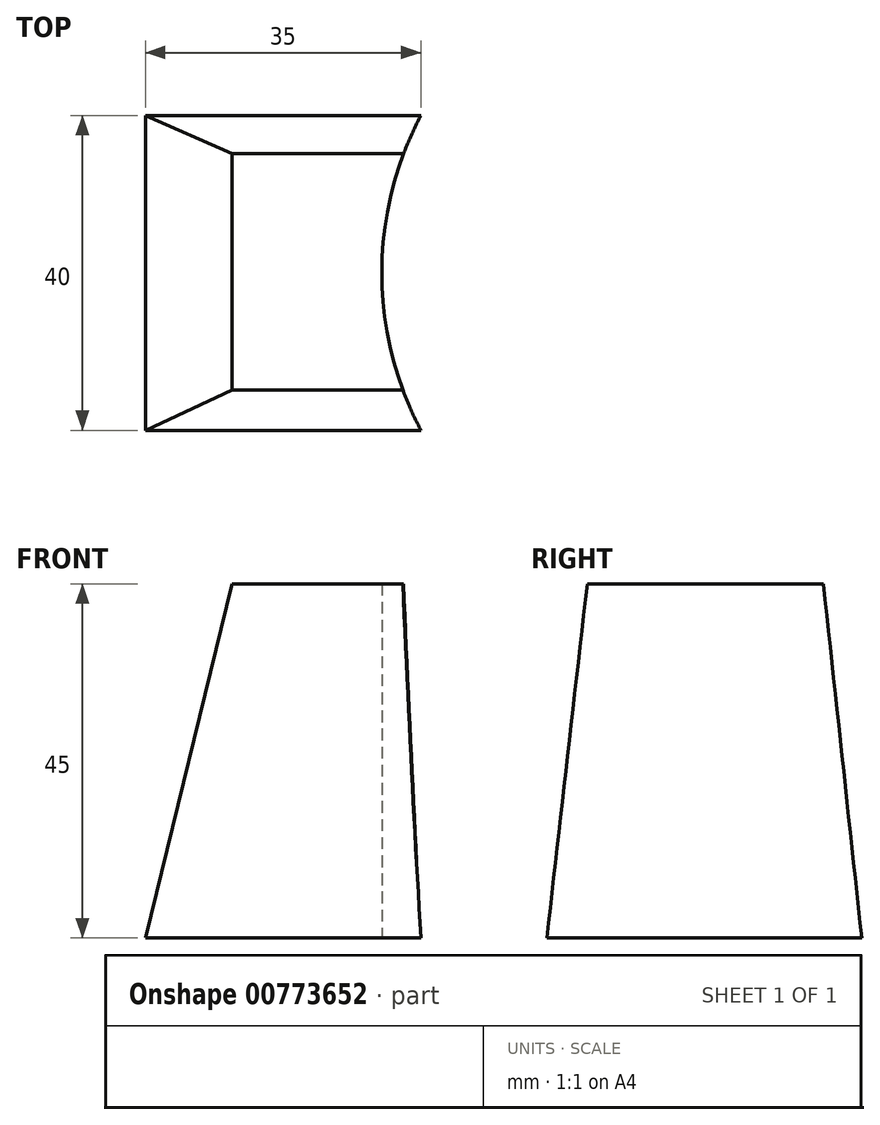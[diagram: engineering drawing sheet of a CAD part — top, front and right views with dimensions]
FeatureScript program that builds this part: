
annotation { "Feature Type Name" : "Feature", "Feature Type Description" : "" }
export const myFeature = defineFeature(function(context is Context, id is Id, definition is map)
    precondition{}
    {
        {
            var Q0;
            Q0=qCreatedBy(makeId("Right.planeOp"),FACE);
            var sketch = newSketch(context, id + "F0", { "sketchPlane" : qUnion([Q0])});
            skLineSegment(sketch, "E0", {"start": v(0, 0) * mm, "end": v(40, 0) * mm});
            skLineSegment(sketch, "E1", {"start": v(40, 0) * mm, "end": v(35.13, 45) * mm});
            skLineSegment(sketch, "E2", {"start": v(35.13, 45) * mm, "end": v(5.13, 45) * mm});
            skLineSegment(sketch, "E3", {"start": v(5.13, 45) * mm, "end": v(0, 0) * mm});
            skSolve(sketch);
        }
        {
            var Q0;
            Q0=makeQuery(id+"F0.imprint","IMPRINT",FACE,{"disambiguationData":[TD([[makeQuery(id+"F0.imprint","IMPRINT",EDGE,{"derivedFrom":sQuery(id+"F0.wireOp",EDGE,"E0")}),1.0]])]});
            extrude(context, id + "F1", {"entities" : qUnion([Q0]), "oppositeDirection" : true, "depth" : 35 * mm, "offsetDistance" : 25.4 * mm});
        }
        {
            var Q0;
            Q0=qCreatedBy(makeId("Front.planeOp"),FACE);
            var sketch = newSketch(context, id + "F2", { "sketchPlane" : qUnion([Q0])});
            skLineSegment(sketch, "E4", {"start": v(-35, 0) * mm, "end": v(-24, 45) * mm});
            skLineSegment(sketch, "E5", {"start": v(-24, 45) * mm, "end": v(-35, 45) * mm});
            skLineSegment(sketch, "E6", {"start": v(-35, 45) * mm, "end": v(-35, 0) * mm});
            skSolve(sketch);
        }
        {
            var Q0;
            Q0=makeQuery(id+"F2.imprint","IMPRINT",FACE,{"disambiguationData":[TD([[makeQuery(id+"F2.imprint","IMPRINT",EDGE,{"derivedFrom":sQuery(id+"F2.wireOp",EDGE,"E4")}),1.0]])]});
            extrude(context, id + "F3", {"entities" : qUnion([Q0]), "operationType" : NewBodyOperationType.REMOVE, "endBound" : BoundingType.THROUGH_ALL, "oppositeDirection" : true, "depth" : 25.4 * mm, "offsetDistance" : 25.4 * mm});
        }
        {
            var Q0;
            Q0=qCreatedBy(makeId("Top.planeOp"),FACE);
            var sketch = newSketch(context, id + "F4", { "sketchPlane" : qUnion([Q0])});
            skArc(sketch, "E7", {"start": v(0, 40) * mm, "mid": v(-4.97, 20) * mm, "end": v(0, 0) * mm});
            skLineSegment(sketch, "E8", {"start": v(0, 40) * mm, "end": v(0, 0) * mm});
            skSolve(sketch);
        }
        {
            var Q0;
            Q0=makeQuery(id+"F4.imprint","IMPRINT",FACE,{"disambiguationData":[TD([[makeQuery(id+"F4.imprint","IMPRINT",EDGE,{"derivedFrom":sQuery(id+"F4.wireOp",EDGE,"E7")}),1.0]])]});
            extrude(context, id + "F5", {"entities" : qUnion([Q0]), "operationType" : NewBodyOperationType.REMOVE, "endBound" : BoundingType.THROUGH_ALL, "depth" : 25.4 * mm, "offsetDistance" : 25.4 * mm});
        }
    });
